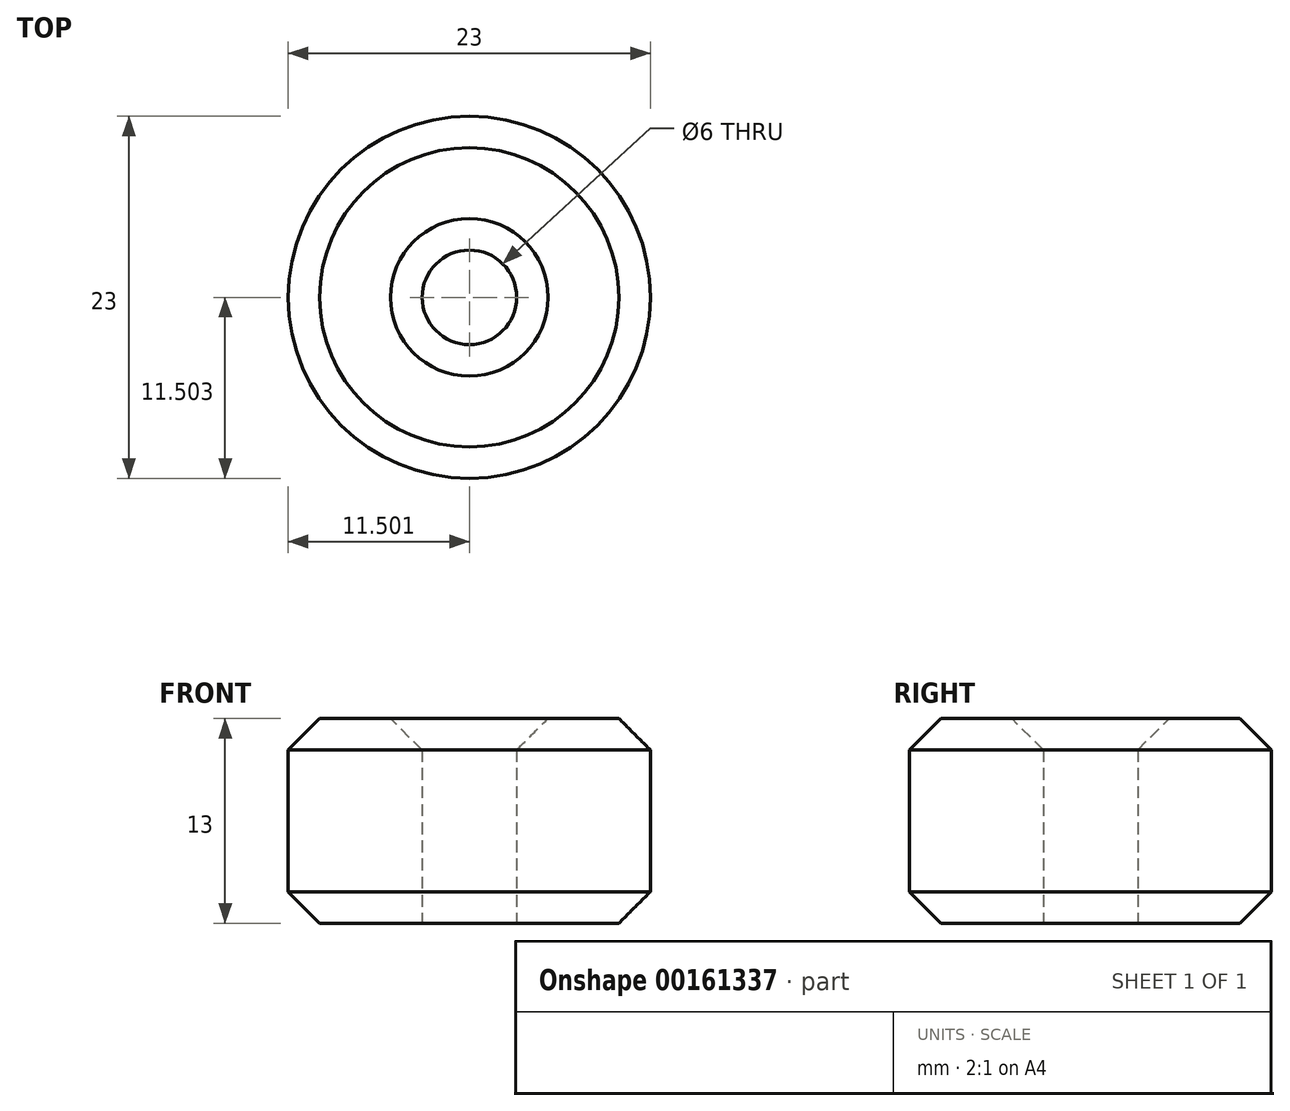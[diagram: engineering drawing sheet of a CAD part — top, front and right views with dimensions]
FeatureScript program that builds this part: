
annotation { "Feature Type Name" : "Feature", "Feature Type Description" : "" }
export const myFeature = defineFeature(function(context is Context, id is Id, definition is map)
    precondition{}
    {
        {
            var Q0;
            Q0=qCreatedBy(makeId("Top.planeOp"),FACE);
            var sketch = newSketch(context, id + "F0", { "sketchPlane" : qUnion([Q0])});
            skCircle(sketch, "E0", {"center": v(-42.8, 37.47) * mm, "radius": 11.5 * mm});
            skCircle(sketch, "E1", {"center": v(-42.8, 37.47) * mm, "radius": 3 * mm});
            skSolve(sketch);
        }
        {
            var Q0;
            Q0=makeQuery(id+"F0.imprint","IMPRINT",FACE,{"disambiguationData":[TD([[makeQuery(id+"F0.imprint","IMPRINT",EDGE,{"derivedFrom":sQuery(id+"F0.wireOp",EDGE,"E0")}),1.0]])]});
            extrude(context, id + "F1", {"entities" : qUnion([Q0]), "depth" : 13 * mm});
        }
        {
            var Q0;
            Q0=makeQuery(id+"F1.opExtrude","CAP_EDGE",EDGE,{"disambiguationData":[OSD([sQuery(id+"F0.wireOp",EDGE,"E0")])],"isStart":false});
            chamfer(context, id + "F2", {"entities" : qUnion([Q0]), "width" : 2 * mm, "tangentPropagation" : true});
        }
        {
            var Q0;
            Q0=makeQuery(id+"F1.opExtrude","CAP_EDGE",EDGE,{"disambiguationData":[OSD([sQuery(id+"F0.wireOp",EDGE,"E0")])],"isStart":true});
            chamfer(context, id + "F3", {"entities" : qUnion([Q0]), "width" : 2 * mm, "tangentPropagation" : true});
        }
        {
            var Q0;
            Q0=makeQuery(id+"F1.opExtrude","CAP_EDGE",EDGE,{"disambiguationData":[OSD([sQuery(id+"F0.wireOp",EDGE,"E1")])],"isStart":false});
            chamfer(context, id + "F4", {"entities" : qUnion([Q0]), "width" : 2 * mm, "tangentPropagation" : true});
        }
    });
